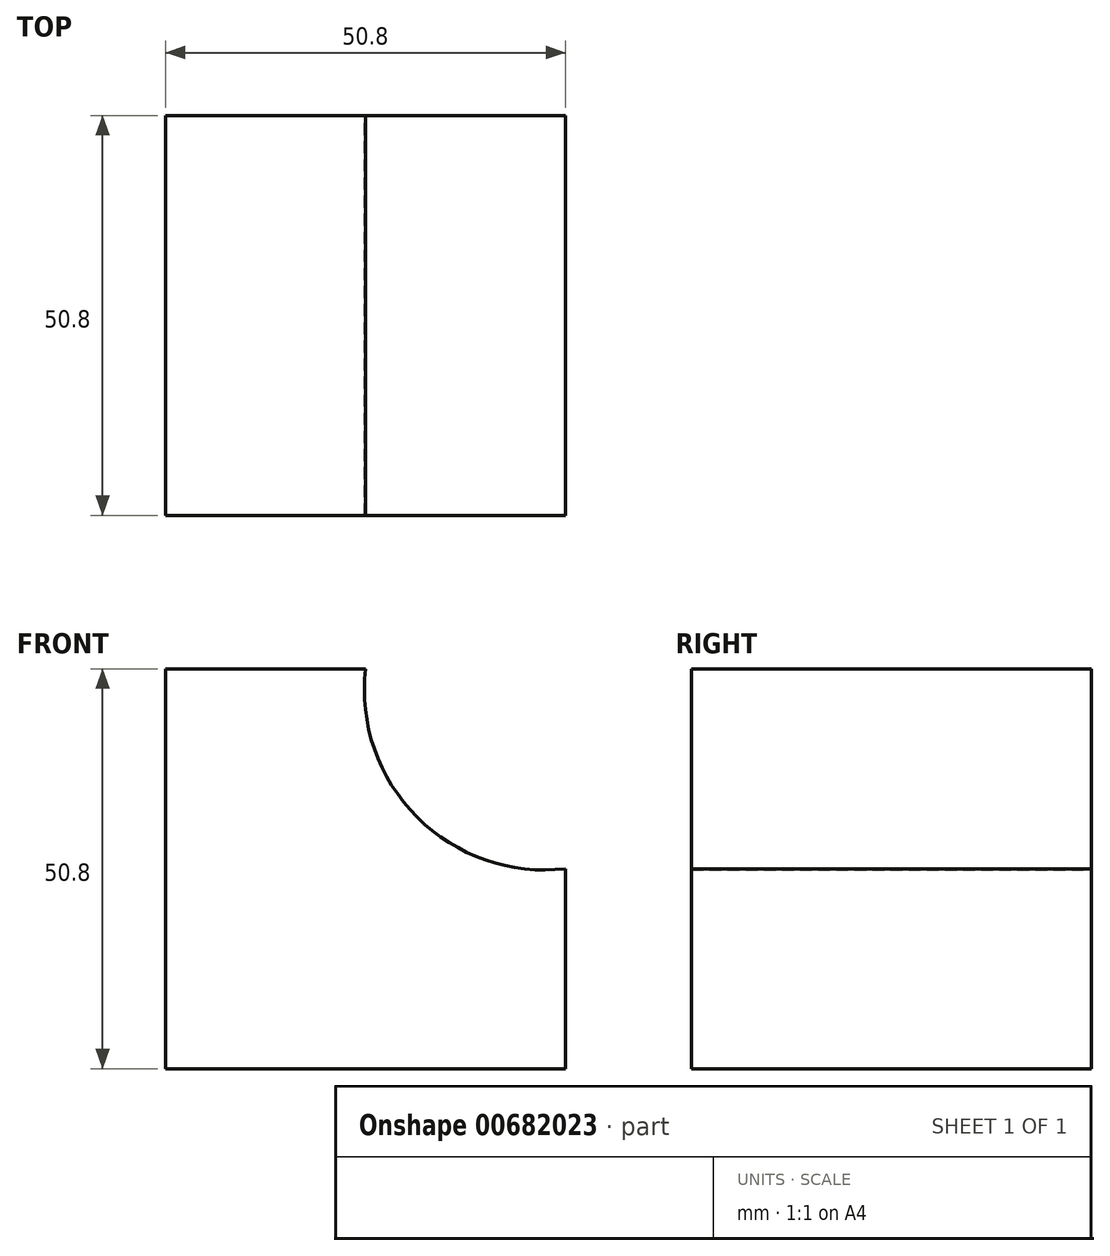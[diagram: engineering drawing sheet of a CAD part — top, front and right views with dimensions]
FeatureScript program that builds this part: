
annotation { "Feature Type Name" : "Feature", "Feature Type Description" : "" }
export const myFeature = defineFeature(function(context is Context, id is Id, definition is map)
    precondition{}
    {
        {
            var Q0;
            Q0=qCreatedBy(makeId("Front.planeOp"),FACE);
            var sketch = newSketch(context, id + "F0", { "sketchPlane" : qUnion([Q0])});
            skLineSegment(sketch, "E0", {"start": v(-31.75, 58.69) * mm, "end": v(-57.15, 58.69) * mm});
            skLineSegment(sketch, "E1", {"start": v(-57.15, 58.69) * mm, "end": v(-57.15, 7.89) * mm});
            skLineSegment(sketch, "E2", {"start": v(-57.15, 7.89) * mm, "end": v(-6.35, 7.89) * mm});
            skLineSegment(sketch, "E3", {"start": v(-6.35, 7.89) * mm, "end": v(-6.35, 33.29) * mm});
            skArc(sketch, "E4", {"start": v(-31.75, 58.69) * mm, "mid": v(-25.2, 39.84) * mm, "end": v(-6.35, 33.29) * mm});
            skSolve(sketch);
        }
        {
            var Q0;
            Q0 = qSketchRegion(id + "F0", true);
            extrude(context, id + "F1", {"entities" : qUnion([Q0]), "depth" : 50.8 * mm, "offsetDistance" : 25.4 * mm});
        }
    });
